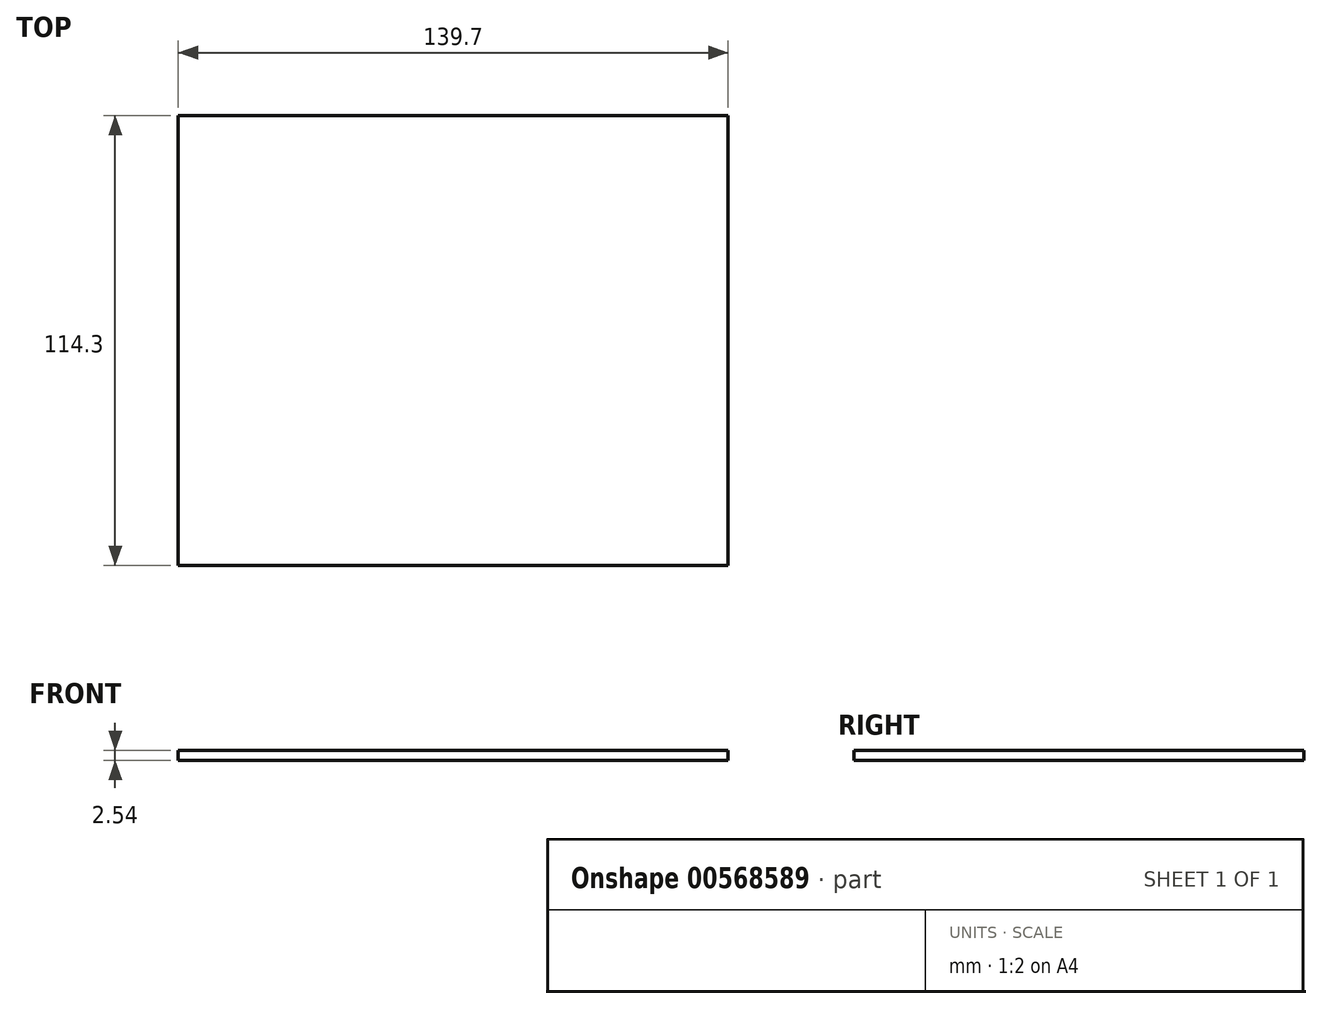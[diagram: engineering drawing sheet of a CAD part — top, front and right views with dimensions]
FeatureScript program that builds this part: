
annotation { "Feature Type Name" : "Feature", "Feature Type Description" : "" }
export const myFeature = defineFeature(function(context is Context, id is Id, definition is map)
    precondition{}
    {
        {
            var Q0;
            Q0=qCreatedBy(makeId("Top.planeOp"),FACE);
            var sketch = newSketch(context, id + "F0", { "sketchPlane" : qUnion([Q0])});
            skLineSegment(sketch, "E0.bottom", {"start": v(-82.76, 51.66) * mm, "end": v(56.94, 51.66) * mm});
            skLineSegment(sketch, "E0.top", {"start": v(-82.76, -62.64) * mm, "end": v(56.94, -62.64) * mm});
            skLineSegment(sketch, "E0.left", {"start": v(-82.76, 51.66) * mm, "end": v(-82.76, -62.64) * mm});
            skLineSegment(sketch, "E0.right", {"start": v(56.94, 51.66) * mm, "end": v(56.94, -62.64) * mm});
            skSolve(sketch);
        }
        {
            var Q0;
            Q0 = qSketchRegion(id + "F0", true);
            extrude(context, id + "F1", {"entities" : qUnion([Q0]), "depth" : 2.54 * mm, "offsetDistance" : 25.4 * mm});
        }
    });
